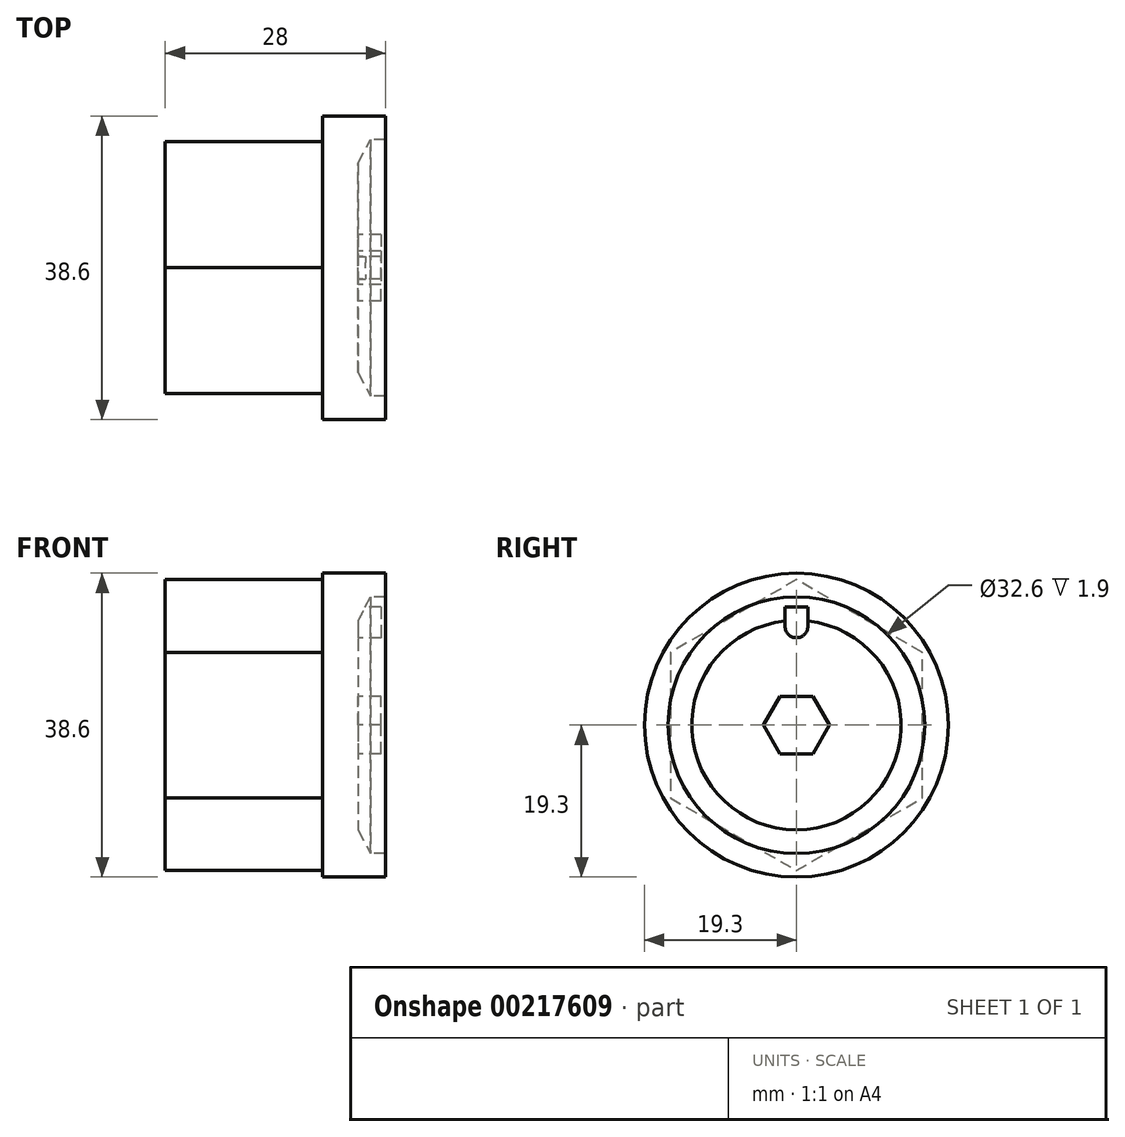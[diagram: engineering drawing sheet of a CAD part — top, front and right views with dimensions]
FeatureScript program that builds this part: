
annotation { "Feature Type Name" : "Feature", "Feature Type Description" : "" }
export const myFeature = defineFeature(function(context is Context, id is Id, definition is map)
    precondition{}
    {
        {
            var Q0;
            Q0=qCreatedBy(makeId("Front.planeOp"),FACE);
            var sketch = newSketch(context, id + "F0", { "sketchPlane" : qUnion([Q0])});
            skLineSegment(sketch, "E0", {"start": v(3.5, 16.3) * mm, "end": v(1.6, 16.3) * mm});
            skLineSegment(sketch, "E1", {"start": v(1.6, 16.3) * mm, "end": v(0, 13.3) * mm});
            skLineSegment(sketch, "E2", {"start": v(-4.5, 19.3) * mm, "end": v(3.5, 19.3) * mm});
            skLineSegment(sketch, "E3", {"start": v(3.5, 19.3) * mm, "end": v(3.5, 16.3) * mm});
            skPoint(sketch, "E4", {"position": v(0, 0) * mm});
            skLineSegment(sketch, "E5", {"start": v(-32.17, 0) * mm, "end": v(62.81, 0) * mm, "construction": true});
            skLineSegment(sketch, "E6", {"start": v(-4.5, 19.3) * mm, "end": v(-4.5, 0) * mm});
            skLineSegment(sketch, "E7", {"start": v(-4.5, 0) * mm, "end": v(0, 0) * mm});
            skLineSegment(sketch, "E8", {"start": v(0, 13.3) * mm, "end": v(0, 0) * mm});
            skSolve(sketch);
        }
        {
            var Q0;
            Q0=makeQuery(id+"F0.imprint","IMPRINT",FACE,{"disambiguationData":[TD([[makeQuery(id+"F0.imprint","IMPRINT",EDGE,{"derivedFrom":sQuery(id+"F0.wireOp",EDGE,"E0")}),-1.0]])]});
            var Q1;
            Q1=sQuery(id+"F0.wireOp",EDGE,"E5");
            revolve(context, id + "F1", {"entities" : qUnion([Q0]), "axis" : qUnion([Q1]), "revolveType" : RevolveType.FULL});
        }
        {
            var Q0;
            Q0=makeQuery(id+"F1.opRevolve","SWEPT_FACE",FACE,{"disambiguationData":[OSD([sQuery(id+"F0.wireOp",EDGE,"E8")])]});
            var sketch = newSketch(context, id + "F2", { "sketchPlane" : qUnion([Q0])});
            skCircle(sketch, "E9.cCircle", {"center": v(0, 0) * mm, "radius": 3.65 * mm, "construction": true});
            skLineSegment(sketch, "E9.0", {"start": v(-4.21, 0) * mm, "end": v(-2.1, 3.65) * mm});
            skLineSegment(sketch, "E9.1", {"start": v(-2.1, 3.65) * mm, "end": v(2.1, 3.65) * mm});
            skLineSegment(sketch, "E9.2", {"start": v(2.1, 3.65) * mm, "end": v(4.21, 0) * mm});
            skLineSegment(sketch, "E9.3", {"start": v(4.21, 0) * mm, "end": v(2.1, -3.65) * mm});
            skLineSegment(sketch, "E9.4", {"start": v(2.1, -3.65) * mm, "end": v(-2.1, -3.65) * mm});
            skLineSegment(sketch, "E9.5", {"start": v(-2.1, -3.65) * mm, "end": v(-4.21, 0) * mm});
            skSolve(sketch);
        }
        {
            var Q0;
            Q0 = qSketchRegion(id + "F2", true);
            extrude(context, id + "F3", {"entities" : qUnion([Q0]), "operationType" : NewBodyOperationType.ADD, "depth" : 2.9 * mm});
        }
        {
            var Q0;
            Q0=makeQuery(id+"F1.opRevolve","SWEPT_FACE",FACE,{"disambiguationData":[OSD([sQuery(id+"F0.wireOp",EDGE,"E6")])]});
            var sketch = newSketch(context, id + "F4", { "sketchPlane" : qUnion([Q0])});
            skCircle(sketch, "E10.cCircle", {"center": v(0, 0) * mm, "radius": 16 * mm, "construction": true});
            skLineSegment(sketch, "E10.0", {"start": v(-16, 9.24) * mm, "end": v(0, 18.48) * mm});
            skLineSegment(sketch, "E10.1", {"start": v(0, 18.48) * mm, "end": v(16, 9.24) * mm});
            skLineSegment(sketch, "E10.2", {"start": v(16, 9.24) * mm, "end": v(16, -9.24) * mm});
            skLineSegment(sketch, "E10.3", {"start": v(16, -9.24) * mm, "end": v(0, -18.48) * mm});
            skLineSegment(sketch, "E10.4", {"start": v(0, -18.48) * mm, "end": v(-16, -9.24) * mm});
            skLineSegment(sketch, "E10.5", {"start": v(-16, -9.24) * mm, "end": v(-16, 9.24) * mm});
            skPoint(sketch, "E10.0.midPoint", {"position": v(-8, 13.86) * mm});
            skSolve(sketch);
        }
        {
            var Q0;
            Q0 = qSketchRegion(id + "F4", true);
            extrude(context, id + "F5", {"entities" : qUnion([Q0]), "operationType" : NewBodyOperationType.ADD, "depth" : 20 * mm});
        }
        {
            var Q0;
            Q0=makeQuery(id+"F1.opRevolve","SWEPT_FACE",FACE,{"disambiguationData":[OSD([sQuery(id+"F0.wireOp",EDGE,"E8")])]});
            var sketch = newSketch(context, id + "F6", { "sketchPlane" : qUnion([Q0])});
            skLineSegment(sketch, "E11", {"start": v(-1.45, 15) * mm, "end": v(1.45, 15) * mm});
            skLineSegment(sketch, "E12", {"start": v(1.45, 15) * mm, "end": v(1.45, 12.55) * mm});
            skLineSegment(sketch, "E13", {"start": v(-1.45, 15) * mm, "end": v(-1.45, 12.55) * mm});
            skArc(sketch, "E14", {"start": v(-1.45, 12.55) * mm, "mid": v(0, 11.1) * mm, "end": v(1.45, 12.55) * mm});
            skPoint(sketch, "E15", {"position": v(0, 15) * mm});
            skSolve(sketch);
        }
        {
            var Q0;
            Q0 = qSketchRegion(id + "F6", true);
            extrude(context, id + "F7", {"entities" : qUnion([Q0]), "operationType" : NewBodyOperationType.ADD, "depth" : 2.9 * mm});
        }
    });
